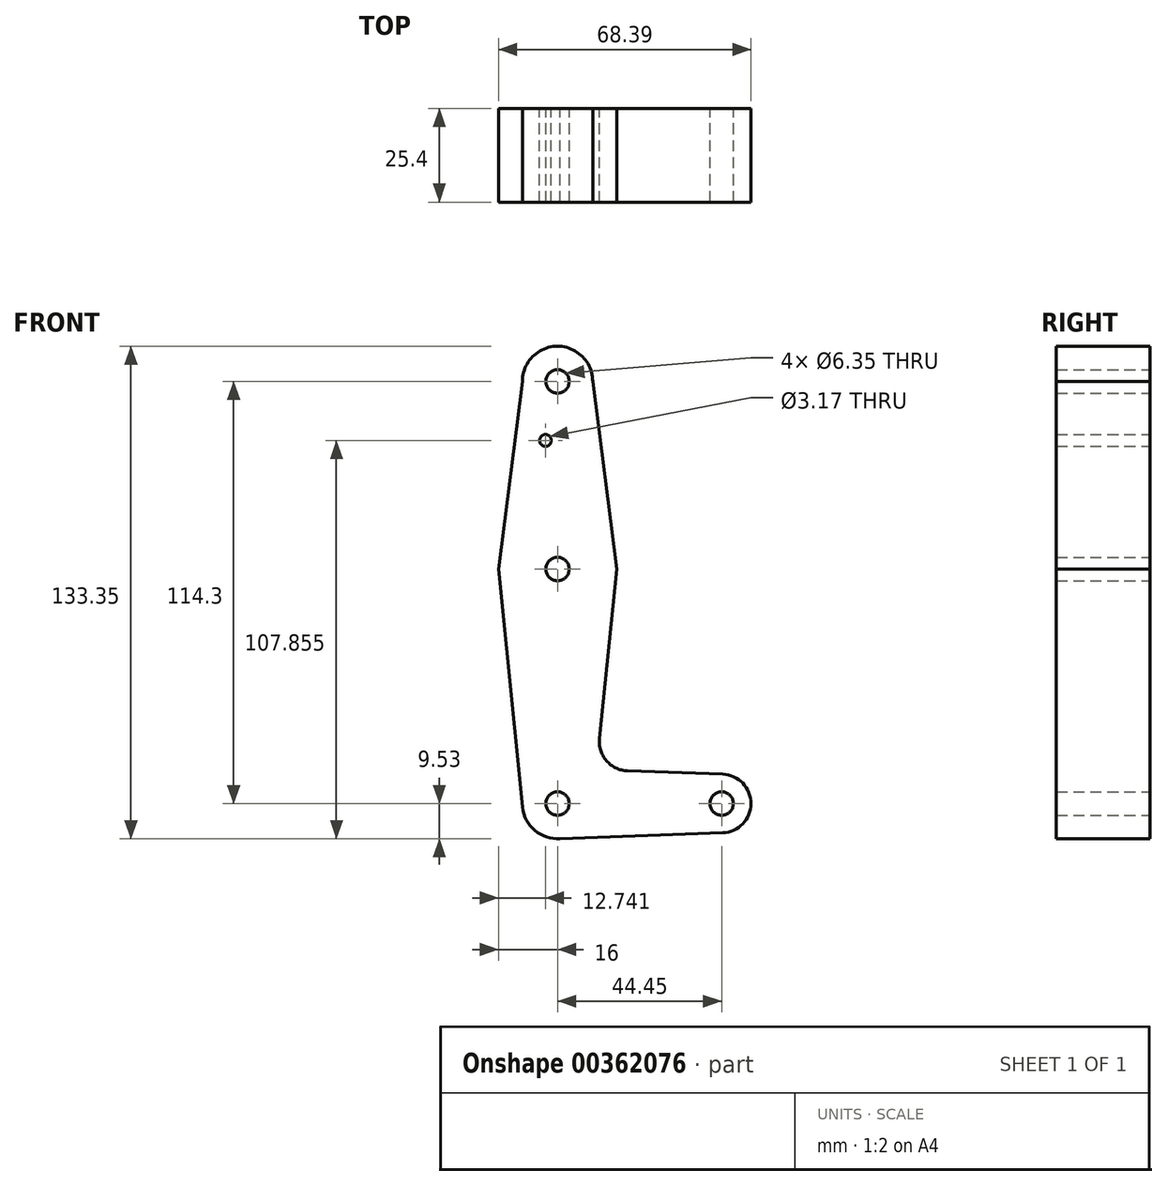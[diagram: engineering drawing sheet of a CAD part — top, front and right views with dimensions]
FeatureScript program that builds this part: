
annotation { "Feature Type Name" : "Feature", "Feature Type Description" : "" }
export const myFeature = defineFeature(function(context is Context, id is Id, definition is map)
    precondition{}
    {
        {
            var Q0;
            Q0=qCreatedBy(makeId("Front.planeOp"),FACE);
            var sketch = newSketch(context, id + "F0", { "sketchPlane" : qUnion([Q0])});
            skLineSegment(sketch, "E0", {"start": v(0, 50.8) * mm, "end": v(0, -63.5) * mm, "construction": true});
            skLineSegment(sketch, "E1", {"start": v(0, -63.5) * mm, "end": v(44.45, -63.5) * mm, "construction": true});
            skCircle(sketch, "E2", {"center": v(0, 50.8) * mm, "radius": 9.53 * mm});
            skCircle(sketch, "E3", {"center": v(0, -63.5) * mm, "radius": 9.53 * mm});
            skCircle(sketch, "E4", {"center": v(44.45, -63.5) * mm, "radius": 7.94 * mm});
            skCircle(sketch, "E5", {"center": v(0, 0) * mm, "radius": 15.88 * mm});
            skLineSegment(sketch, "E6", {"start": v(-9.52, 50.76) * mm, "end": v(-16, 0) * mm});
            skLineSegment(sketch, "E7", {"start": v(-16, 0) * mm, "end": v(-9.48, -64.46) * mm});
            skLineSegment(sketch, "E8", {"start": v(9.52, 50.77) * mm, "end": v(16, 0) * mm});
            skLineSegment(sketch, "E9", {"start": v(0, -73.03) * mm, "end": v(44.73, -71.43) * mm});
            skLineSegment(sketch, "E10", {"start": v(16, 0) * mm, "end": v(11.36, -45.9) * mm});
            skLineSegment(sketch, "E11", {"start": v(18.98, -54.65) * mm, "end": v(44.73, -55.57) * mm});
            skLineSegment(sketch, "E12", {"start": v(0, 0) * mm, "end": v(0, -63.5) * mm});
            skCircle(sketch, "E13", {"center": v(0, 50.8) * mm, "radius": 3.18 * mm});
            skCircle(sketch, "E14", {"center": v(0, -63.5) * mm, "radius": 3.18 * mm});
            skCircle(sketch, "E15", {"center": v(44.45, -63.5) * mm, "radius": 3.18 * mm});
            skCircle(sketch, "E16", {"center": v(0, 0) * mm, "radius": 3.18 * mm});
            skPoint(sketch, "E17.newPointB", {"position": v(0, -53.98) * mm});
            skArc(sketch, "E17.filletArc", {"start": v(11.36, -45.9) * mm, "mid": v(13.27, -51.93) * mm, "end": v(18.98, -54.65) * mm});
            skCircle(sketch, "E18", {"center": v(-3.26, 34.82) * mm, "radius": 1.59 * mm});
            skSolve(sketch);
        }
        {
            var Q0;
            Q0 = qSketchRegion(id + "F0", true);
            extrude(context, id + "F1", {"entities" : qUnion([Q0]), "depth" : 25.4 * mm});
        }
    });
